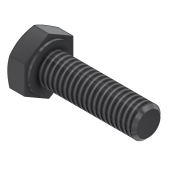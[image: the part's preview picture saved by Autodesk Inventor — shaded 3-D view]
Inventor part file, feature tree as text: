
AUTODESK INVENTOR PART (.ipt)
format: ipt  version: 2015 (Build 190159000, 159)  size: 219,136 bytes
history: native  units: mm
features: sketch x4, revolve x2, extrude x2, thread x1
ambient origin geometry x8: Origin, YZ Plane, XZ Plane, XY Plane, X Axis, Y Axis, Z Axis, Center Point
bodies: Solid1 (feature_tree)
feature tree (9):
  revolve  "Revolution1"  [1 undecoded]
  extrude  "Extrusion1"  Depth=8.9mm
  revolve  "Revolution2"  Angle=45.0deg
  thread  "Thread1"  [1 undecoded]
  extrude  "Extrusion2"  TaperAngle=90.0deg  [1 undecoded]
  sketch  "Sketch1"  dims[d0=6.0mm d1=20.0mm]
  sketch  "Sketch2"  dims[d2=10.0mm d3=8.9mm]
  sketch  "Sketch3"  dims[d4=4.0mm d5=45.0deg d6=4.77mm]
  sketch  "Sketch4"  dims[d7=0.5mm d8=90.0deg d9=10.0mm d10=0.0mm d11=11.1mm d12=1.11mm d13=30.0deg d14=90.0deg d15=10.0mm d16=0.0mm d17=7.5mm d18=0.1mm d19=0.0mm]
note: 3 required parameter values undecoded (feature->parameter linkage not recoverable at this tier; creation-order binding heuristic only, values carry confidence <= 0.55)